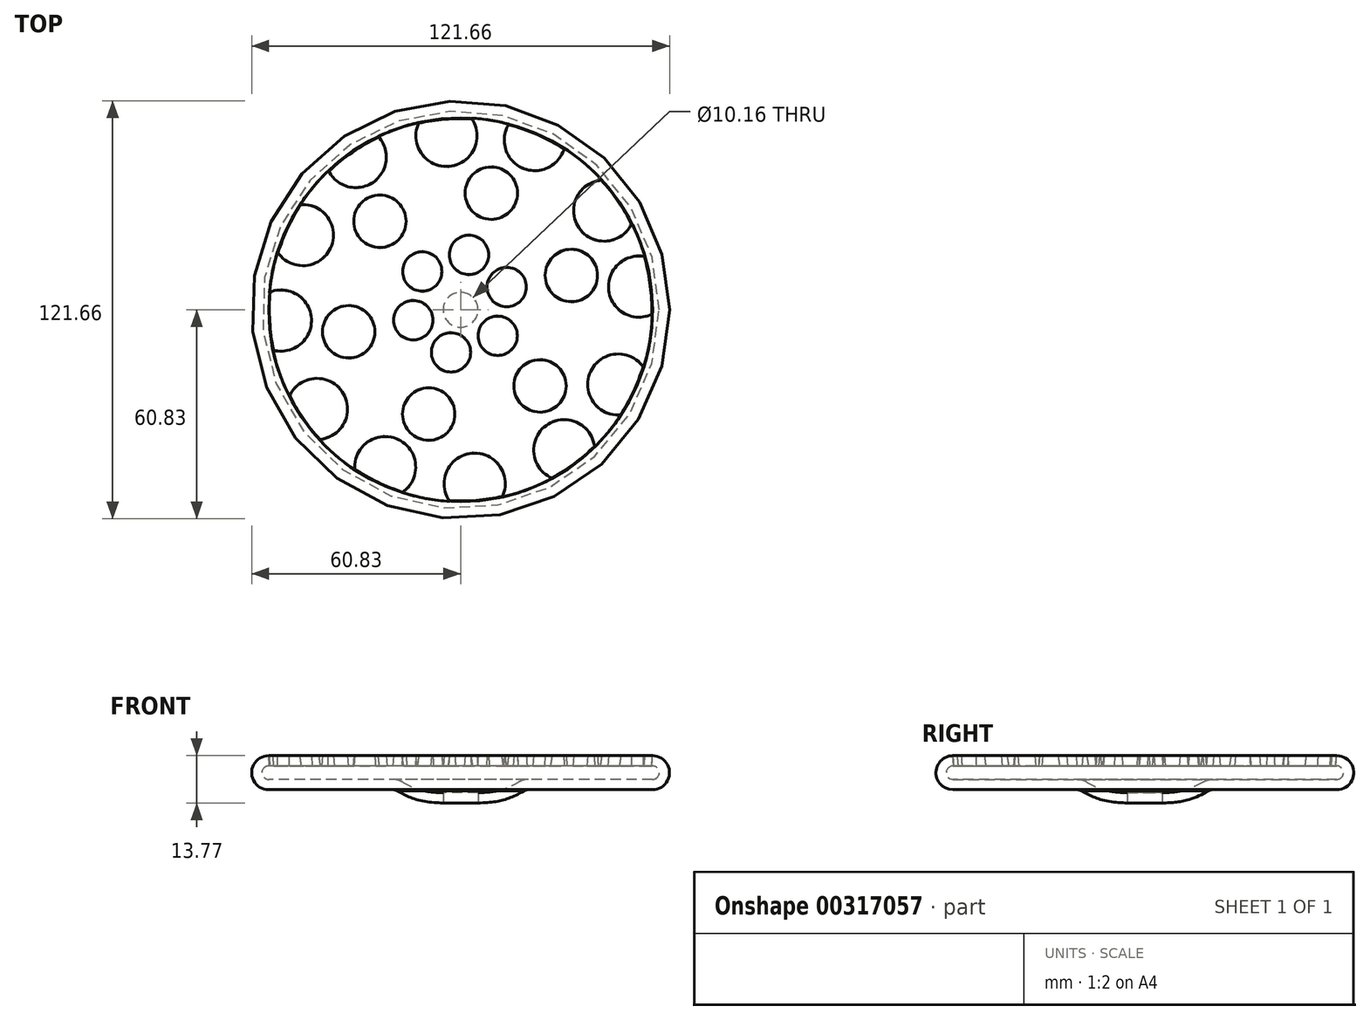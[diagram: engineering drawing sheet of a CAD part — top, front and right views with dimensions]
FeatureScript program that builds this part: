
annotation { "Feature Type Name" : "Feature", "Feature Type Description" : "" }
export const myFeature = defineFeature(function(context is Context, id is Id, definition is map)
    precondition{}
    {
        {
            var Q0;
            Q0=qCreatedBy(makeId("Front.planeOp"),FACE);
            var sketch = newSketch(context, id + "F0", { "sketchPlane" : qUnion([Q0])});
            skLineSegment(sketch, "E0.bottom", {"start": v(0, 0) * mm, "end": v(55.88, 0) * mm});
            skLineSegment(sketch, "E0.top", {"start": v(0, 9.9) * mm, "end": v(55.88, 9.9) * mm});
            skLineSegment(sketch, "E0.left", {"start": v(0, 0) * mm, "end": v(0, 9.9) * mm});
            skLineSegment(sketch, "E0.right", {"start": v(55.88, 0) * mm, "end": v(55.88, 9.9) * mm});
            skArc(sketch, "E1", {"start": v(55.88, 0) * mm, "mid": v(60.83, 4.95) * mm, "end": v(55.88, 9.9) * mm});
            skPoint(sketch, "E2", {"position": v(19.05, 0) * mm});
            skFitSpline(sketch, "E3", {"points": [v(0, -3.91) * mm, v(19.05, 0) * mm], "startDerivative": vector(29.49, 0) * mm, "endDerivative": vector(19.05, 11.18) * mm});
            skLineSegment(sketch, "E4", {"start": v(0, -3.91) * mm, "end": v(0, 0) * mm});
            skLineSegment(sketch, "E5", {"start": v(0, 22.1) * mm, "end": v(0, -17.04) * mm, "construction": true});
            skSolve(sketch);
        }
        {
            var Q0;
            Q0 = qSketchRegion(id + "F0", true);
            var Q1;
            Q1=sQuery(id+"F0.wireOp",EDGE,"E5");
            revolve(context, id + "F1", {"entities" : qUnion([Q0]), "axis" : qUnion([Q1]), "revolveType" : RevolveType.FULL});
        }
        {
            var Q0;
            Q0=makeQuery(id+"F1.opRevolve","SWEPT_EDGE",EDGE,{"disambiguationData":[OSD([sQuery(id+"F0.wireOp",EDGE,"E0.bottom"),sQuery(id+"F0.wireOp",EDGE,"E3")])]});
            fillet(context, id + "F2", {"entities" : qUnion([Q0]), "radius" : 2.54 * mm, "tangentPropagation" : true, "allowEdgeOverflow" : false});
        }
        {
            var Q0;
            Q0=makeQuery(id+"F1.opRevolve","SWEPT_FACE",FACE,{"disambiguationData":[OSD([sQuery(id+"F0.wireOp",EDGE,"E0.top")])]});
            var Q1;
            Q1=makeQuery(id+"F1.opRevolve","SWEPT_BODY",BODY,{"disambiguationData":[OSD([sQuery(id+"F0.wireOp",EDGE,"E0.bottom"),sQuery(id+"F0.wireOp",EDGE,"E0.top"),sQuery(id+"F0.wireOp",EDGE,"E0.left"),sQuery(id+"F0.wireOp",EDGE,"E1"),sQuery(id+"F0.wireOp",EDGE,"E3"),sQuery(id+"F0.wireOp",EDGE,"E4")])]});
            shell(context, id + "F3", {"isHollow" : true, "entities" : qUnion([Q0]), "parts" : qUnion([Q1]), "thickness" : 3 * mm});
        }
        {
            var Q0;
            Q0=makeQuery(id+"F1.opRevolve","SWEPT_FACE",FACE,{"disambiguationData":[OSD([sQuery(id+"F0.wireOp",EDGE,"E0.top")])]});
            var sketch = newSketch(context, id + "F4", { "sketchPlane" : qUnion([Q0])});
            skCircle(sketch, "E6.0", {"center": v(0, 0) * mm, "radius": 55.88 * mm});
            skSolve(sketch);
        }
        {
            var Q0;
            Q0=makeQuery(id+"F1.opRevolve","SWEPT_FACE",FACE,{"disambiguationData":[OSD([sQuery(id+"F0.wireOp",EDGE,"E0.top")])]});
            var sketch = newSketch(context, id + "F5", { "sketchPlane" : qUnion([Q0])});
            skFitSpline(sketch, "E7", {"points": [v(0, 0) * mm, v(-27.03, -48.9) * mm], "startDerivative": vector(-13.58, -68.7) * mm, "endDerivative": vector(-49.3, -25.08) * mm});
            skCircle(sketch, "E8", {"center": v(0, 0) * mm, "radius": 31.75 * mm, "construction": true});
            skCircle(sketch, "E9", {"center": v(0, 0) * mm, "radius": 12.7 * mm, "construction": true});
            skCircle(sketch, "E10", {"center": v(0, 0) * mm, "radius": 50.8 * mm, "construction": true});
            skCircle(sketch, "E11", {"center": v(-2.79, -12.39) * mm, "radius": 5.72 * mm});
            skCircle(sketch, "E12", {"center": v(-9.28, -30.36) * mm, "radius": 7.62 * mm});
            skArc(sketch, "E13", {"start": v(-17.04, -53.22) * mm, "mid": v(-18.11, -37.8) * mm, "end": v(-30.8, -46.62) * mm});
            skCircle(sketch, "E14.1.0", {"center": v(10.81, -7.56) * mm, "radius": 5.72 * mm});
            skCircle(sketch, "E14.1.1", {"center": v(23.13, -22.17) * mm, "radius": 7.62 * mm});
            skArc(sketch, "E14.1.2", {"start": v(39.02, -40) * mm, "mid": v(24.9, -33.72) * mm, "end": v(26.74, -49.07) * mm});
            skCircle(sketch, "E14.2.0", {"center": v(13.43, 6.63) * mm, "radius": 5.72 * mm});
            skCircle(sketch, "E14.2.1", {"center": v(32.24, 10) * mm, "radius": 7.62 * mm});
            skArc(sketch, "E14.2.2", {"start": v(53.7, 15.46) * mm, "mid": v(43.14, 5.6) * mm, "end": v(55.87, -1.24) * mm});
            skCircle(sketch, "E14.3.0", {"center": v(2.45, 16) * mm, "radius": 5.72 * mm});
            skCircle(sketch, "E14.3.1", {"center": v(8.94, 33.97) * mm, "radius": 7.62 * mm});
            skArc(sketch, "E14.3.2", {"start": v(14.05, 54.09) * mm, "mid": v(18.05, 41.27) * mm, "end": v(30.18, 47.03) * mm});
            skCircle(sketch, "E14.4.0", {"center": v(-11.15, 11.17) * mm, "radius": 5.72 * mm});
            skCircle(sketch, "E14.4.1", {"center": v(-23.48, 25.77) * mm, "radius": 7.62 * mm});
            skArc(sketch, "E14.4.2", {"start": v(-38.48, 40.52) * mm, "mid": v(-25.48, 37.14) * mm, "end": v(-23.96, 50.48) * mm});
            skCircle(sketch, "E14.5.0", {"center": v(-13.77, -3.03) * mm, "radius": 5.72 * mm});
            skCircle(sketch, "E14.5.1", {"center": v(-32.58, -6.4) * mm, "radius": 7.62 * mm});
            skArc(sketch, "E14.5.2", {"start": v(-54.64, -11.71) * mm, "mid": v(-43.42, -2.6) * mm, "end": v(-55.65, 5.1) * mm});
            skPoint(sketch, "E14.center", {"position": v(-0.17, 1.8) * mm});
            skLineSegment(sketch, "E15", {"start": v(-21.95, -45.81) * mm, "end": v(30.17, -40.87) * mm, "construction": true});
            skPoint(sketch, "E16", {"position": v(4.1, -43.34) * mm});
            skLineSegment(sketch, "E17", {"start": v(0, 0) * mm, "end": v(4.1, -50.63) * mm, "construction": true});
            skArc(sketch, "E18", {"start": v(12.09, -54.56) * mm, "mid": v(3.39, -41.77) * mm, "end": v(-3.13, -55.8) * mm});
            skArc(sketch, "E19.1.0", {"start": v(53.3, -16.81) * mm, "mid": v(37.87, -17.95) * mm, "end": v(46.75, -30.6) * mm});
            skArc(sketch, "E19.2.0", {"start": v(41.2, 37.75) * mm, "mid": v(34.48, 23.82) * mm, "end": v(49.88, 25.18) * mm});
            skArc(sketch, "E19.3.0", {"start": v(-12.09, 54.56) * mm, "mid": v(-3.39, 41.77) * mm, "end": v(3.13, 55.8) * mm});
            skArc(sketch, "E19.4.0", {"start": v(-53.3, 16.81) * mm, "mid": v(-37.87, 17.95) * mm, "end": v(-46.75, 30.6) * mm});
            skArc(sketch, "E19.5.0", {"start": v(-41.2, -37.75) * mm, "mid": v(-34.48, -23.82) * mm, "end": v(-49.88, -25.18) * mm});
            skCircle(sketch, "E20.0", {"center": v(0, 0) * mm, "radius": 55.88 * mm});
            skSolve(sketch);
        }
        {
            var Q0;
            Q0 = qSketchRegion(id + "F4", true);
            extrude(context, id + "F6", {"entities" : qUnion([Q0]), "operationType" : NewBodyOperationType.REMOVE, "endBound" : BoundingType.UP_TO_NEXT, "oppositeDirection" : true, "depth" : 25.4 * mm, "hasDraft" : true, "draftAngle" : 4 * degree, "draftPullDirection" : true});
        }
        {
            var Q0;
            Q0=makeQuery(id+"F5.imprint","IMPRINT",FACE,{"disambiguationData":[TD([[makeQuery(id+"F5.imprint","IMPRINT",EDGE,{"derivedFrom":sQuery(id+"F5.wireOp",EDGE,"E14.1.0")}),-1.0]])]});
            extrude(context, id + "F7", {"entities" : qUnion([Q0]), "oppositeDirection" : true, "depth" : 3 * mm, "hasDraft" : true, "draftAngle" : 4 * degree, "draftPullDirection" : true});
        }
        {
            var Q0;
            Q0=makeQuery(id+"F1.opRevolve","SWEPT_FACE",FACE,{"disambiguationData":[OSD([sQuery(id+"F0.wireOp",EDGE,"E0.bottom")])]});
            cPlane(context, id + "F8", {"entities" : qUnion([Q0]), "cplaneType" : CPlaneType.OFFSET, "offset" : 3.91 * mm, "width" : 152.4 * mm, "height" : 152.4 * mm});
        }
        {
            var Q0;
            Q0=qCreatedBy(id+"F8.planeOp",FACE);
            var sketch = newSketch(context, id + "F9", { "sketchPlane" : qUnion([Q0])});
            skCircle(sketch, "E21", {"center": v(0, 0) * mm, "radius": 5.08 * mm});
            skSolve(sketch);
        }
        {
            var Q0;
            Q0 = qSketchRegion(id + "F9", true);
            extrude(context, id + "F10", {"entities" : qUnion([Q0]), "operationType" : NewBodyOperationType.REMOVE, "oppositeDirection" : true, "depth" : 6.35 * mm});
        }
    });
